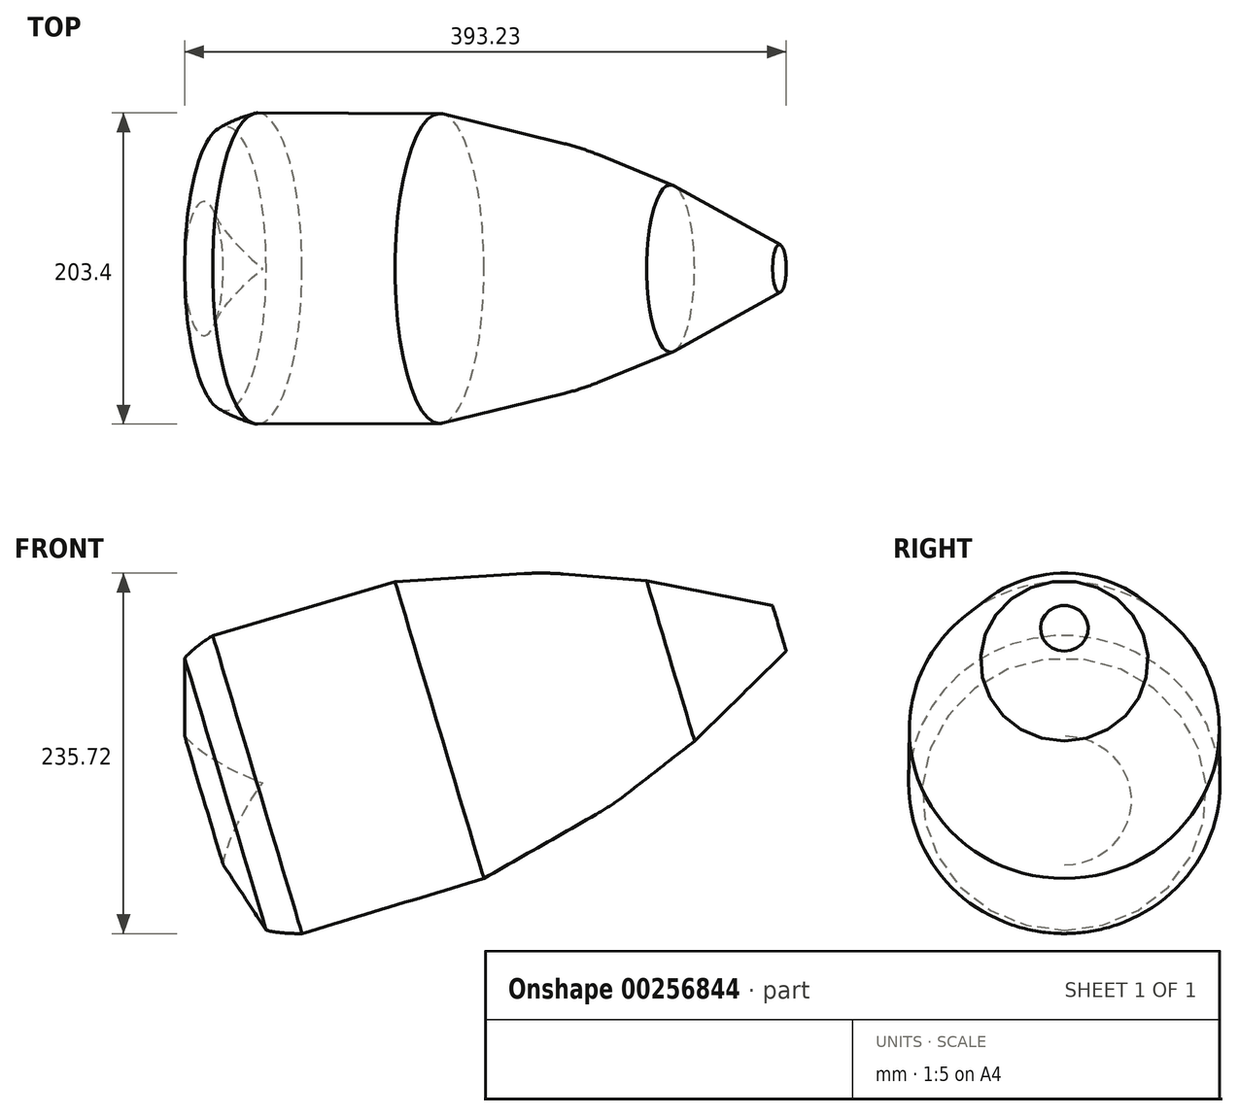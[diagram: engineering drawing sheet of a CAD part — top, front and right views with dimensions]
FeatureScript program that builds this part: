
annotation { "Feature Type Name" : "Feature", "Feature Type Description" : "" }
export const myFeature = defineFeature(function(context is Context, id is Id, definition is map)
    precondition{}
    {
        {
            var Q0;
            Q0=qCreatedBy(makeId("Front.planeOp"),FACE);
            var sketch = newSketch(context, id + "F0", { "sketchPlane" : qUnion([Q0])});
            skEllipse(sketch, "E0", {"center": v(-97.34, 6.19) * mm, "majorRadius": 250.16 * mm, "minorRadius": 84.76 * mm, "majorAxis": v(-1, 0)});
            skLineSegment(sketch, "E1", {"start": v(90.15, 62.3) * mm, "end": v(-284.83, -49.93) * mm});
            skLineSegment(sketch, "E2", {"start": v(81.33, 59.67) * mm, "end": v(-76.8, 90.67) * mm});
            skLineSegment(sketch, "E3", {"start": v(-335.81, 31.8) * mm, "end": v(-335.81, -19.42) * mm});
            skLineSegment(sketch, "E4", {"start": v(48.48, 66.1) * mm, "end": v(52.95, 51.17) * mm});
            skLineSegment(sketch, "E5", {"start": v(-33.92, 82.26) * mm, "end": v(-131.1, 90.18) * mm});
            skLineSegment(sketch, "E6", {"start": v(-131.1, 90.18) * mm, "end": v(-101.2, 87.74) * mm});
            skLineSegment(sketch, "E7", {"start": v(-101.2, 87.74) * mm, "end": v(-217.28, 80.57) * mm});
            skLineSegment(sketch, "E8", {"start": v(-217.28, 80.57) * mm, "end": v(-198.34, 81.74) * mm});
            skLineSegment(sketch, "E9", {"start": v(-198.34, 81.74) * mm, "end": v(-317.47, 46.46) * mm});
            skSolve(sketch);
        }
        {
            var Q0;
            {var subQ6=sQuery(id+"F0.wireOp",EDGE,"E3");Q0=makeQuery(id+"F0.imprint","IMPRINT",FACE,{"disambiguationData":[TD([[makeQuery(id+"F0.imprint","IMPRINT",EDGE,{"derivedFrom":subQ6}),1.0]])]});}
            var Q1;
            Q1=sQuery(id+"F0.wireOp",EDGE,"E1");
            revolve(context, id + "F1", {"entities" : qUnion([Q0]), "axis" : qUnion([Q1]), "revolveType" : RevolveType.FULL});
        }
        {
            var Q0;
            Q0=makeQuery(id+"F1.opRevolve","SWEPT_EDGE",EDGE,{"disambiguationData":[OSD([sQuery(id+"F0.wireOp",EDGE,"E5"),sQuery(id+"F0.wireOp",EDGE,"E6"),sQuery(id+"F0.wireOp",EDGE,"E7")])]});
            fillet(context, id + "F2", {"entities" : qUnion([Q0]), "radius" : 177.8 * mm, "tangentPropagation" : true, "allowEdgeOverflow" : false});
        }
    });
